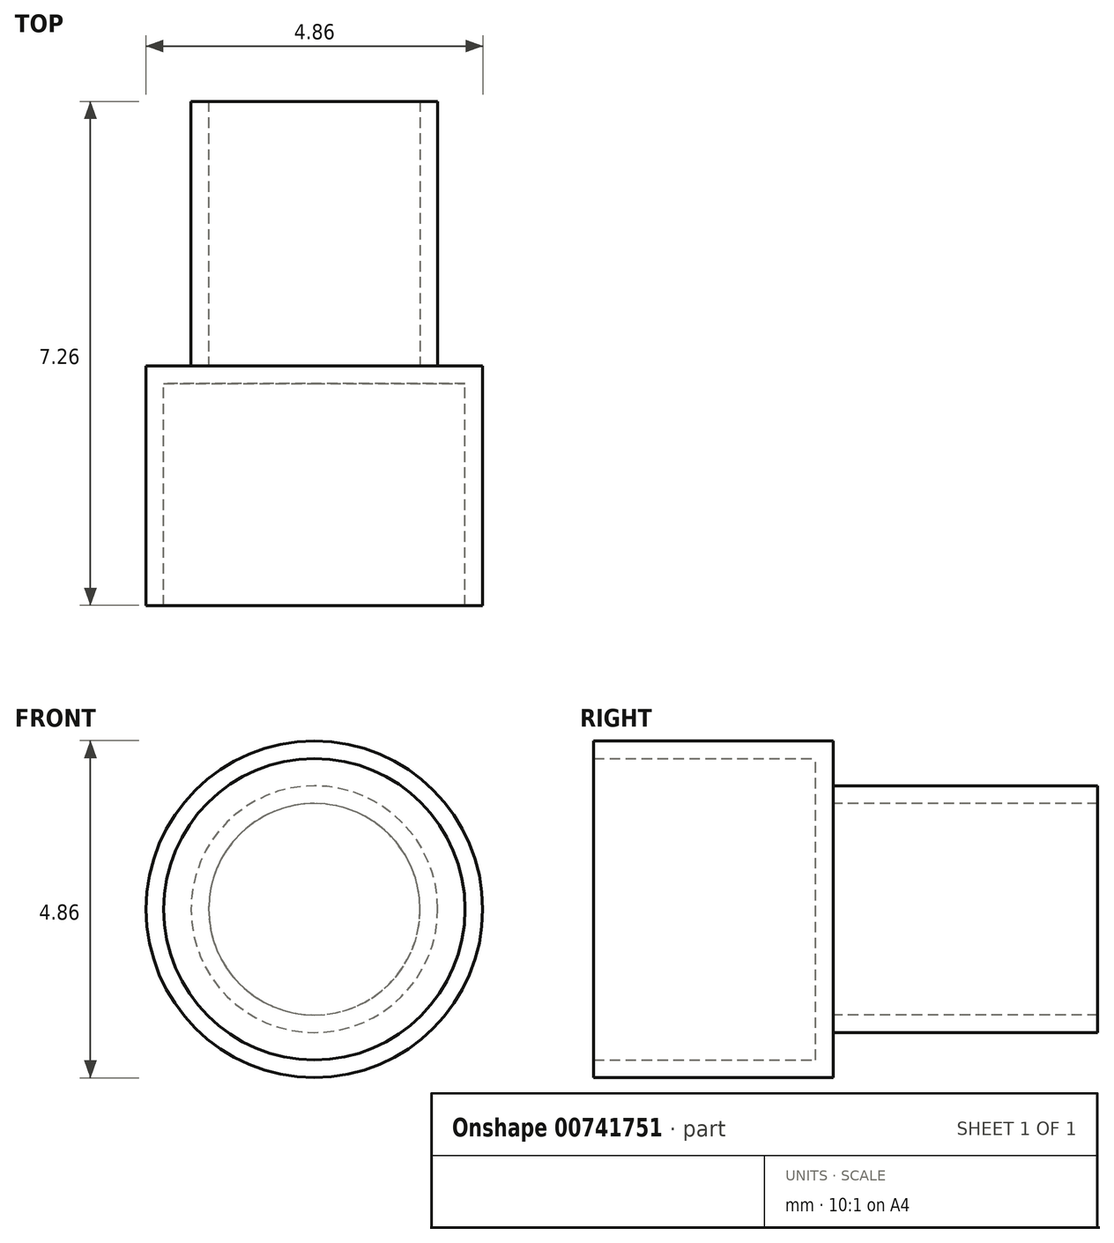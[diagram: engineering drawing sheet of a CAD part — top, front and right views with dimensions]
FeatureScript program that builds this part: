
annotation { "Feature Type Name" : "Feature", "Feature Type Description" : "" }
export const myFeature = defineFeature(function(context is Context, id is Id, definition is map)
    precondition{}
    {
        {
            var Q0;
            Q0=qCreatedBy(makeId("Front.planeOp"),FACE);
            var sketch = newSketch(context, id + "F0", { "sketchPlane" : qUnion([Q0])});
            skCircle(sketch, "E0", {"center": v(0, 0) * mm, "radius": 2.43 * mm});
            skSolve(sketch);
        }
        {
            var Q0;
            Q0 = qSketchRegion(id + "F0", true);
            extrude(context, id + "F1", {"entities" : qUnion([Q0]), "depth" : 3.45 * mm, "offsetDistance" : 25.4 * mm});
        }
        {
            var Q0;
            Q0=makeQuery(id+"F1.opExtrude","CAP_FACE",FACE,{"disambiguationData":[OSD([sQuery(id+"F0.wireOp",EDGE,"E0")])],"isStart":false});
            shell(context, id + "F2", {"entities" : qUnion([Q0]), "thickness" : 0.25 * mm});
        }
        {
            var Q0;
            Q0=makeQuery(id+"F1.opExtrude","CAP_FACE",FACE,{"disambiguationData":[OSD([sQuery(id+"F0.wireOp",EDGE,"E0")])],"isStart":true});
            var sketch = newSketch(context, id + "F3", { "sketchPlane" : qUnion([Q0])});
            skCircle(sketch, "E1", {"center": v(0, 0) * mm, "radius": 1.78 * mm});
            skSolve(sketch);
        }
        {
            var Q0;
            Q0=makeQuery(id+"F3.imprint","IMPRINT",FACE,{"disambiguationData":[TD([[makeQuery(id+"F3.imprint","IMPRINT",EDGE,{"derivedFrom":sQuery(id+"F3.wireOp",EDGE,"E1")}),1.0]])]});
            extrude(context, id + "F4", {"entities" : qUnion([Q0]), "operationType" : NewBodyOperationType.ADD, "depth" : 3.8 * mm, "offsetDistance" : 25.4 * mm});
        }
        {
            var Q0;
            Q0=makeQuery(id+"F4.opExtrude","CAP_FACE",FACE,{"disambiguationData":[OSD([sQuery(id+"F3.wireOp",EDGE,"E1")])],"isStart":false});
            shell(context, id + "F5", {"entities" : qUnion([Q0]), "thickness" : 0.25 * mm});
        }
    });
